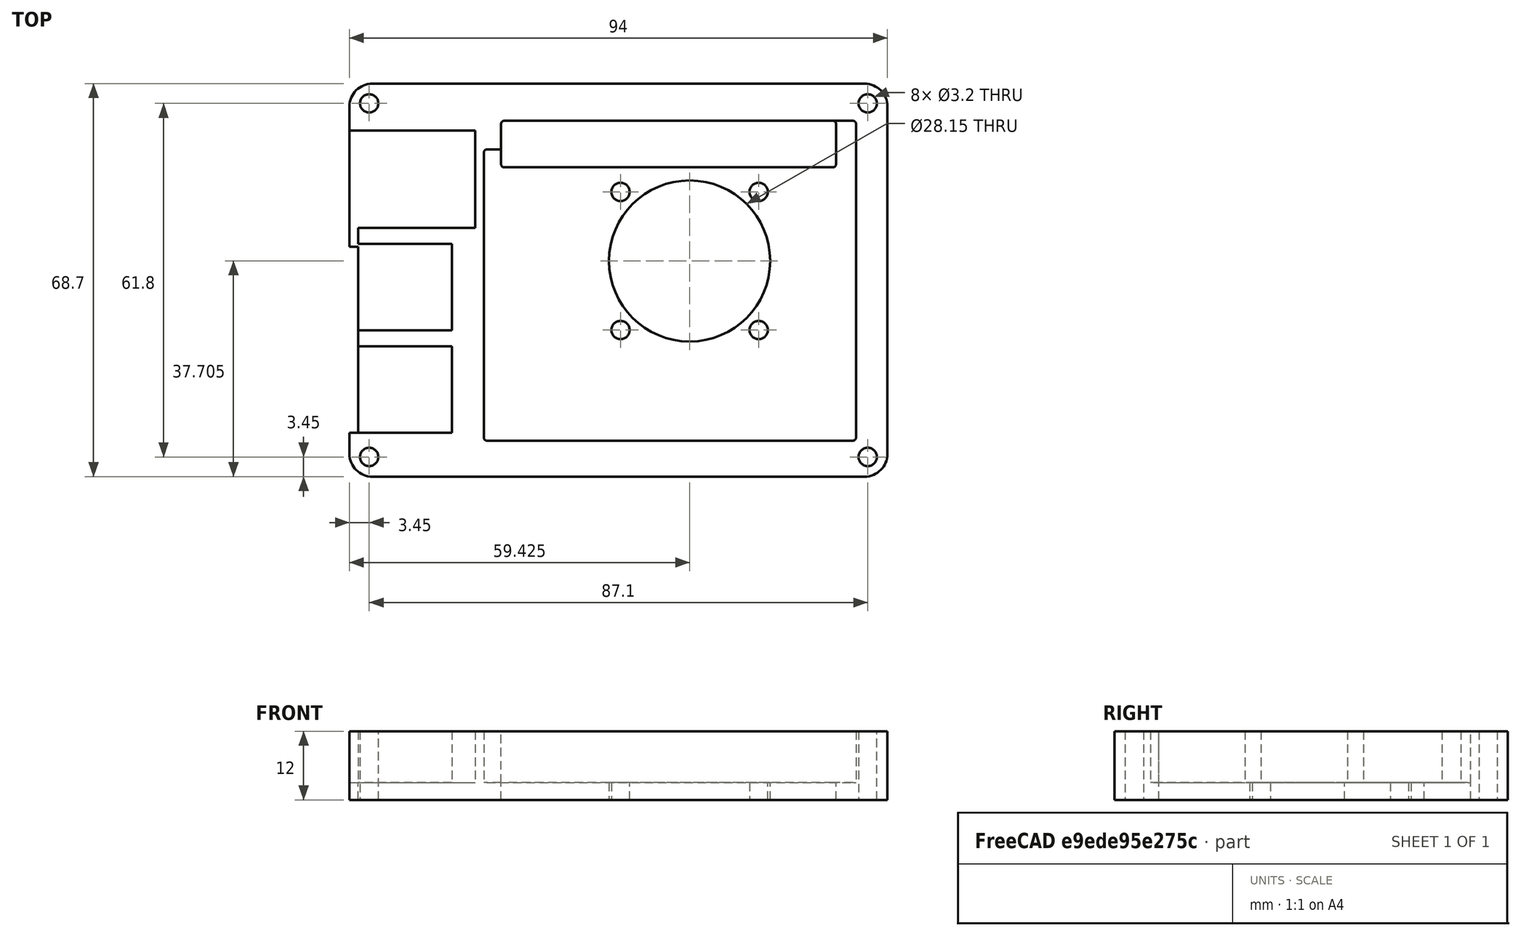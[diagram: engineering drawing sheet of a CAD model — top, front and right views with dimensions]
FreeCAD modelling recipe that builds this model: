
FCSTD DOCUMENT  (FreeCAD 0.19R24267 +148 (Git))
Label: 1. Lage
License: All rights reserved
LicenseURL: http://en.wikipedia.org/wiki/All_rights_reserved
objects: TechDraw::DrawViewDimension×21, TechDraw::DrawProjGroupItem×4, Sketcher::SketchObject×2, PartDesign::Fillet×2, PartDesign::Pad×1, PartDesign::Pocket×1, PartDesign::Body×1, TechDraw::DrawSVGTemplate×1, TechDraw::DrawProjGroup×1, TechDraw::DrawPage×1
note: 11 computed .brp shape members not serialized (recipe doc carries the construction recipe); baked Part::Feature solids carry a one-line shape summary decoded from their .brp

FEATURE [Sketcher::SketchObject] Sketch
  FullyConstrained = true
  MapMode = 5
  Support = -> [XY_Plane]
  sketch-geometry (29):
    g0: LineSegment StartX=0 StartY=0 StartZ=0 EndX=94 EndY=0 EndZ=0
    g1: LineSegment StartX=94 StartY=0 StartZ=0 EndX=94 EndY=68.7 EndZ=0
    g2: LineSegment StartX=94 StartY=68.7 StartZ=0 EndX=0 EndY=68.7 EndZ=0
    g3: Circle CenterX=3.45 CenterY=65.25 CenterZ=0 NormalX=0 NormalY=0 NormalZ=1 AngleXU=0 Radius=1.6
    g4: Circle CenterX=90.55 CenterY=65.25 CenterZ=0 NormalX=0 NormalY=0 NormalZ=1 AngleXU=0 Radius=1.6
    g5: Circle CenterX=90.55 CenterY=3.45 CenterZ=0 NormalX=0 NormalY=0 NormalZ=1 AngleXU=0 Radius=1.6
    g6: Circle CenterX=3.45 CenterY=3.45 CenterZ=0 NormalX=0 NormalY=0 NormalZ=1 AngleXU=0 Radius=1.6
    g7: GeomPoint X=47 Y=34.35 Z=0
    g8: LineSegment StartX=26.5 StartY=62.2 StartZ=0 EndX=85 EndY=62.2 EndZ=0
    g9: LineSegment StartX=85 StartY=62.2 StartZ=0 EndX=85 EndY=54.08 EndZ=0
    g10: LineSegment StartX=85 StartY=54.08 StartZ=0 EndX=26.5 EndY=54.08 EndZ=0
    g11: LineSegment StartX=26.5 StartY=54.08 StartZ=0 EndX=26.5 EndY=62.2 EndZ=0
    g12: LineSegment StartX=45.35 StartY=51.78 StartZ=0 EndX=73.5 EndY=51.78 EndZ=0
    g13: LineSegment StartX=73.5 StartY=51.78 StartZ=0 EndX=73.5 EndY=23.63 EndZ=0
    g14: LineSegment StartX=73.5 StartY=23.63 StartZ=0 EndX=45.35 EndY=23.63 EndZ=0
    g15: LineSegment StartX=45.35 StartY=23.63 StartZ=0 EndX=45.35 EndY=51.78 EndZ=0
    g16: Circle CenterX=59.425 CenterY=37.705 CenterZ=0 NormalX=0 NormalY=0 NormalZ=1 AngleXU=0 Radius=14.075
    g17: Circle CenterX=47.3512 CenterY=25.6312 CenterZ=0 NormalX=0 NormalY=0 NormalZ=1 AngleXU=0 Radius=1.6
    g18: Circle CenterX=71.4988 CenterY=25.6312 CenterZ=0 NormalX=0 NormalY=0 NormalZ=1 AngleXU=0 Radius=1.6
    g19: Circle CenterX=71.4988 CenterY=49.7788 CenterZ=0 NormalX=0 NormalY=0 NormalZ=1 AngleXU=0 Radius=1.6
    g20: Circle CenterX=47.3512 CenterY=49.7788 CenterZ=0 NormalX=0 NormalY=0 NormalZ=1 AngleXU=0 Radius=1.6
    g21: LineSegment StartX=45.35 StartY=51.78 StartZ=0 EndX=59.425 EndY=37.705 EndZ=0
    g22: GeomPoint X=48.4825 Y=48.6475 Z=0
    g23: GeomPoint X=49.4725 Y=47.6575 Z=0
    g24: LineSegment StartX=0 StartY=68.7 StartZ=0 EndX=0 EndY=40.2 EndZ=0
    g25: LineSegment StartX=0 StartY=40.2 StartZ=0 EndX=1.5 EndY=40.2 EndZ=0
    g26: LineSegment StartX=1.5 StartY=40.2 StartZ=0 EndX=1.5 EndY=7.7 EndZ=0
    g27: LineSegment StartX=1.5 StartY=7.7 StartZ=0 EndX=0 EndY=7.7 EndZ=0
    g28: LineSegment StartX=0 StartY=7.7 StartZ=0 EndX=0 EndY=0 EndZ=0
  constraints (76):
    c: Coincident(g0,g1)
    c: Coincident(g1,g2)
    c: Horizontal(g0)
    c: Horizontal(g2)
    c: Vertical(g1)
    c: Coincident(g0,g-1)
    c: DistanceY(g0,g2) = 68.7
    c: DistanceX(g2,g2) = 94
    c: Equal(g3,g4)
    c: Equal(g4,g6)
    c: Equal(g6,g5)
    c: Symmetric(g6,g4,g7)
    c: Symmetric(g5,g3,g7)
    c: Symmetric(g0,g2,g7)
    c: Horizontal(g6,g5)
    c: Vertical(g6,g3)
    c: Radius(g6) = 1.6
    c: DistanceY(g0,g6) = 3.45
    c: DistanceX(g0,g6) = 3.45
    c: Coincident(g8,g9)
    c: Coincident(g9,g10)
    c: Coincident(g10,g11)
    c: Coincident(g11,g8)
    c: Horizontal(g8)
    c: Horizontal(g10)
    c: Vertical(g9)
    c: Vertical(g11)
    c: DistanceY(g11,g11) = 8.12
    c: DistanceX(g8,g8) = 58.5
    c: DistanceY(g8,g1) = 6.5
    c: DistanceX(g8,g1) = 9
    c: Coincident(g12,g13)
    c: Coincident(g13,g14)
    c: Coincident(g14,g15)
    c: Coincident(g15,g12)
    c: Horizontal(g12)
    c: Horizontal(g14)
    c: Vertical(g13)
    c: Vertical(g15)
    c: Equal(g13,g14)
    c: Tangent(g16,g13)
    c: Symmetric(g12,g13,g16)
    c: Radius(g16) = 14.075
    c: DistanceY(g12,g9) = 2.3
    c: DistanceX(g13,g0) = 20.5
    c: Equal(g20,g17)
    c: Equal(g17,g18)
    c: Equal(g18,g19)
    c: Symmetric(g19,g17,g16)
    c: Symmetric(g18,g20,g16)
    c: Horizontal(g20,g19)
    c: Vertical(g20,g17)
    c: Coincident(g21,g12)
    c: Coincident(g21,g16)
    c: PointOnObject(g20,g21)
    c: PointOnObject(g22,g20)
    c: PointOnObject(g22,g21)
    c: PointOnObject(g23,g16)
    c: PointOnObject(g23,g21)
    c: Distance(g23,g22) = 1.4
    c: Radius(g20) = 1.6
    c: Equal(g2,g0)
    c: Coincident(g2,g24)
    c: Vertical(g24)
    c: Horizontal(g25)
    c: Coincident(g25,g26)
    c: Vertical(g26)
    c: Coincident(g26,g27)
    c: PointOnObject(g27,g-2)
    c: Horizontal(g27)
    c: Coincident(g27,g28)
    c: Coincident(g28,g0)
    c: Coincident(g25,g24)
    c: DistanceX(g25,g25) = 1.5
    c: DistanceY(g26,g26) = 32.5
    c: DistanceY(g24,g24) = 28.5
FEATURE [PartDesign::Pad] Pad
  Direction = (1,1,1)
  Length = 12
  Length2 = 100
  Profile = -> Sketch
  Type = 0
FEATURE [PartDesign::Fillet] Fillet
  Base = -> Pad [Edge26,Edge29,Edge32,Edge25]
  BaseFeature = -> Pad
  Radius = 0.5
  SupportTransform = false
FEATURE [PartDesign::Fillet] Fillet001
  Base = -> Fillet [Edge62,Edge61,Edge60,Edge59]
  BaseFeature = -> Fillet
  Radius = 4
  SupportTransform = false
FEATURE [Sketcher::SketchObject] Sketch001
  ExternalGeometry = -> [Fillet001]
  FullyConstrained = true
  MapMode = 5
  Placement = pos=(0,0,12) rot=(0,0,1;0rad)
  Support = -> [Fillet001]
  sketch-geometry (25):
    g0: LineSegment StartX=26.5 StartY=61.7 StartZ=0 EndX=26.5 EndY=57.2 EndZ=0
    g1: LineSegment StartX=24 StartY=6.3 StartZ=0 EndX=88 EndY=6.3 EndZ=0
    g2: LineSegment StartX=26.5 StartY=57.2 StartZ=0 EndX=24 EndY=57.2 EndZ=0
    g3: ArcOfCircle CenterX=24 CenterY=56.7 CenterZ=0 NormalX=0 NormalY=0 NormalZ=1 AngleXU=0 Radius=0.5 StartAngle=1.5708 EndAngle=3.14159
    g4: LineSegment StartX=23.5 StartY=56.7 StartZ=0 EndX=23.5 EndY=6.8 EndZ=0
    g5: ArcOfCircle CenterX=24 CenterY=6.8 CenterZ=0 NormalX=0 NormalY=0 NormalZ=1 AngleXU=0 Radius=0.5 StartAngle=3.14159 EndAngle=4.71239
    g6: ArcOfCircle CenterX=88 CenterY=6.8 CenterZ=0 NormalX=0 NormalY=0 NormalZ=1 AngleXU=0 Radius=0.5 StartAngle=4.71239 EndAngle=6.28319
    g7: LineSegment StartX=88.5 StartY=6.8 StartZ=0 EndX=88.5 EndY=61.7 EndZ=0
    g8: ArcOfCircle CenterX=88 CenterY=61.7 CenterZ=0 NormalX=0 NormalY=0 NormalZ=1 AngleXU=0 Radius=0.5 StartAngle=9e-16 EndAngle=1.5708
    g9: LineSegment StartX=88 StartY=62.2 StartZ=0 EndX=27 EndY=62.2 EndZ=0
    g10: ArcOfCircle CenterX=27 CenterY=61.7 CenterZ=0 NormalX=0 NormalY=0 NormalZ=1 AngleXU=0 Radius=0.5 StartAngle=1.5708 EndAngle=3.14159
    g11: LineSegment StartX=0 StartY=60.5 StartZ=0 EndX=22 EndY=60.5 EndZ=0
    g12: LineSegment StartX=22 StartY=60.5 StartZ=0 EndX=22 EndY=43.5 EndZ=0
    g13: LineSegment StartX=2e-16 StartY=40.2 StartZ=0 EndX=0 EndY=60.5 EndZ=0
    g14: LineSegment StartX=1.5 StartY=40.7 StartZ=0 EndX=17.9 EndY=40.7 EndZ=0
    g15: LineSegment StartX=17.9 StartY=40.7 StartZ=0 EndX=17.9 EndY=25.6 EndZ=0
    g16: LineSegment StartX=17.9 StartY=25.6 StartZ=0 EndX=1.5 EndY=25.6 EndZ=0
    g17: LineSegment StartX=1.5 StartY=22.8 StartZ=0 EndX=17.9 EndY=22.8 EndZ=0
    g18: LineSegment StartX=17.9 StartY=22.8 StartZ=0 EndX=17.9 EndY=7.7 EndZ=0
    g19: LineSegment StartX=17.9 StartY=7.7 StartZ=0 EndX=1.5 EndY=7.7 EndZ=0
    g20: LineSegment StartX=1.5 StartY=7.7 StartZ=0 EndX=1.5 EndY=22.8 EndZ=0
    g21: LineSegment StartX=2e-16 StartY=40.2 StartZ=0 EndX=1.5 EndY=40.2 EndZ=0
    g22: LineSegment StartX=1.5 StartY=43.5 StartZ=0 EndX=22 EndY=43.5 EndZ=0
    g23: LineSegment StartX=1.5 StartY=43.5 StartZ=0 EndX=1.5 EndY=40.7 EndZ=0
    g24: LineSegment StartX=1.5 StartY=40.2 StartZ=0 EndX=1.5 EndY=25.6 EndZ=0
  constraints (72):
    c: Vertical(g0)
    c: Horizontal(g1)
    c: Coincident(g0,g-9)
    c: Coincident(g0,g2)
    c: Horizontal(g2)
    c: Tangent(g2,g3) = -1.5708
    c: Coincident(g3,g4)
    c: Vertical(g4)
    c: Tangent(g4,g5) = -1.5708
    c: Coincident(g5,g1)
    c: Tangent(g1,g6) = -1.5708
    c: Coincident(g6,g7)
    c: Vertical(g7)
    c: Tangent(g7,g8) = -1.5708
    c: Coincident(g8,g9)
    c: Horizontal(g9)
    c: Tangent(g9,g10) = -1.5708
    c: Coincident(g10,g0)
    c: Coincident(g10,g-9)
    c: Equal(g3,g10)
    c: Equal(g5,g3)
    c: Equal(g3,g8)
    c: Equal(g8,g6)
    c: Vertical(g1,g5)
    c: Horizontal(g3,g3)
    c: Vertical(g8,g8)
    c: Horizontal(g6,g6)
    c: DistanceX(g6,g-7) = 5.5
    c: DistanceY(g-6,g1) = 6.3
    c: DistanceX(g3,g0) = 3
    c: DistanceY(g0,g-10) = 11.5
    c: Coincident(g11,g12)
    c: Coincident(g13,g11)
    c: Horizontal(g11)
    c: Vertical(g12)
    c: PointOnObject(g11,g-11)
    c: DistanceX(g11,g11) = 22
    c: DistanceY(g12,g12) = 17
    c: Coincident(g14,g15)
    c: Coincident(g15,g16)
    c: Horizontal(g14)
    c: Horizontal(g16)
    c: Vertical(g15)
    c: Coincident(g17,g18)
    c: Coincident(g18,g19)
    c: Coincident(g19,g20)
    c: Coincident(g20,g17)
    c: Horizontal(g17)
    c: Horizontal(g19)
    c: Vertical(g18)
    c: Vertical(g20)
    c: Coincident(g19,g-12)
    c: Equal(g15,g18)
    c: Equal(g17,g16)
    c: DistanceY(g18,g18) = 15.1
    c: DistanceY(g17,g15) = 2.8
    c: DistanceY(g14,g12) = 2.8
    c: DistanceX(g15,g4) = 5.6
    c: Vertical(g14,g17)
    c: Horizontal(g21)
    c: Coincident(g21,g-11)
    c: Vertical(g21,g-12)
    c: Coincident(g22,g12)
    c: Horizontal(g22)
    c: Coincident(g21,g13)
    c: Coincident(g23,g22)
    c: Coincident(g23,g14)
    c: Vertical(g23)
    c: Coincident(g24,g16)
    c: Vertical(g24)
    c: Vertical(g16,g17)
    c: Horizontal(g24,g13)
FEATURE [PartDesign::Pocket] Pocket
  BaseFeature = -> Fillet001
  Length = 9
  Length2 = 100
  Profile = -> Sketch001
  Type = 0
FEATURE [PartDesign::Body] Body
  Group = -> [Sketch,Pad,Fillet,Fillet001,Sketch001,Pocket]
  Origin = -> Origin
  Tip = -> Pocket
FEATURE [TechDraw::DrawSVGTemplate] Template
  EditableTexts = Designed_by_Name=David Völlm; Drawing_number=Drawing number; FC-Date=23.05.2023; FC-SC=Scale; FC-SH=Sheet; FC-Title=Raspberry Pi Gehäuse; Subtitle=Subtitle; Weight=Weight
  Height = 210
  Orientation = 1
  Width = 297
FEATURE [TechDraw::DrawProjGroupItem] ProjItem  label="Front"
  CoarseView = false
  Direction = (0,0,1)
  Focus = 100
  HardHidden = false
  IsoCount = 0
  IsoHidden = false
  IsoVisible = false
  LockPosition = true
  Perspective = false
  Rotation = 0
  RotationVector = (1,0,0)
  Scale = 0.5
  ScaleType = 2
  SeamHidden = false
  SeamVisible = true
  SmoothHidden = false
  SmoothVisible = true
  Source = -> [Body]
  Type = 0
  X = 0
  XDirection = (1,0,0)
  Y = 0
FEATURE [TechDraw::DrawProjGroupItem] ProjItem001  label="Left"
  CoarseView = false
  Direction = (-1,0,1e-16)
  Focus = 100
  HardHidden = false
  IsoCount = 0
  IsoHidden = false
  IsoVisible = false
  LockPosition = false
  Perspective = false
  Rotation = 0
  RotationVector = (1,0,0)
  ScaleType = 2
  SeamHidden = false
  SeamVisible = true
  SmoothHidden = false
  SmoothVisible = true
  Source = -> [Body]
  Type = 1
  X = 65.2243
  XDirection = (1e-16,0,1)
  Y = 0
FEATURE [TechDraw::DrawProjGroupItem] ProjItem002  label="Bottom"
  CoarseView = false
  Direction = (0,-1,0)
  Focus = 100
  HardHidden = false
  IsoCount = 0
  IsoHidden = false
  IsoVisible = false
  LockPosition = false
  Perspective = false
  Rotation = 0
  RotationVector = (1,0,0)
  ScaleType = 2
  SeamHidden = false
  SeamVisible = true
  SmoothHidden = false
  SmoothVisible = true
  Source = -> [Body]
  Type = 5
  X = 0
  XDirection = (1,0,0)
  Y = 35.175
FEATURE [TechDraw::DrawProjGroupItem] ProjItem003  label="Top"
  CoarseView = false
  Direction = (0,1,0)
  Focus = 100
  HardHidden = false
  IsoCount = 0
  IsoHidden = false
  IsoVisible = false
  LockPosition = false
  Perspective = false
  Rotation = 0
  RotationVector = (1,0,0)
  ScaleType = 2
  SeamHidden = false
  SeamVisible = true
  SmoothHidden = false
  SmoothVisible = true
  Source = -> [Body]
  Type = 4
  X = 0
  XDirection = (1,0,0)
  Y = -55.5576
FEATURE [TechDraw::DrawProjGroup] ProjGroup
  Anchor = -> ProjItem
  AutoDistribute = true
  LockPosition = false
  ProjectionType = 0
  Rotation = 0
  Scale = 0.5
  ScaleType = 2
  Source = -> [Body]
  Views = -> [ProjItem,ProjItem001,ProjItem002,ProjItem003]
  X = 107.356
  Y = 128.807
  spacingX = 15
  spacingY = 15
FEATURE [TechDraw::DrawViewDimension] Dimension001
  Arbitrary = false
  ArbitraryTolerances = false
  EqualTolerance = true
  FormatSpec = R%.2f
  FormatSpecOverTolerance = %+.2f
  FormatSpecUnderTolerance = %+.2f
  Inverted = false
  LockPosition = false
  MeasureType = 1
  OverTolerance = 0
  References2D = -> [ProjItem]
  Rotation = 0
  ScaleType = 0
  TheoreticalExact = false
  Type = 4
  UnderTolerance = 0
  X = -37.7748
  Y = 24.8617
FEATURE [TechDraw::DrawViewDimension] Dimension004
  Arbitrary = false
  ArbitraryTolerances = false
  EqualTolerance = true
  FormatSpec = %.2f
  FormatSpecOverTolerance = %+.2f
  FormatSpecUnderTolerance = %+.2f
  Inverted = false
  LockPosition = false
  MeasureType = 1
  OverTolerance = 0
  References2D = -> [ProjItem]
  Rotation = 0
  ScaleType = 0
  TheoreticalExact = false
  Type = 2
  UnderTolerance = 0
  X = -33.4357
  Y = -8.97918
FEATURE [TechDraw::DrawViewDimension] Dimension005
  Arbitrary = false
  ArbitraryTolerances = false
  EqualTolerance = true
  FormatSpec = %.2f
  FormatSpecOverTolerance = %+.2f
  FormatSpecUnderTolerance = %+.2f
  Inverted = false
  LockPosition = false
  MeasureType = 1
  OverTolerance = 0
  References2D = -> [ProjItem]
  Rotation = 0
  ScaleType = 0
  TheoreticalExact = false
  Type = 2
  UnderTolerance = 0
  X = -41.6257
  Y = -9.94553
FEATURE [TechDraw::DrawViewDimension] Dimension006
  Arbitrary = false
  ArbitraryTolerances = false
  EqualTolerance = true
  FormatSpec = %.2f
  FormatSpecOverTolerance = %+.2f
  FormatSpecUnderTolerance = %+.2f
  Inverted = false
  LockPosition = false
  MeasureType = 1
  OverTolerance = 0
  References2D = -> [ProjItem]
  Rotation = 0
  ScaleType = 0
  TheoreticalExact = false
  Type = 2
  UnderTolerance = 0
  X = -50.9328
  Y = -9.45354
FEATURE [TechDraw::DrawViewDimension] Dimension007
  Arbitrary = false
  ArbitraryTolerances = false
  EqualTolerance = true
  FormatSpec = %.2f
  FormatSpecOverTolerance = %+.2f
  FormatSpecUnderTolerance = %+.2f
  Inverted = false
  LockPosition = false
  MeasureType = 1
  OverTolerance = 0
  References2D = -> [ProjItem]
  Rotation = 0
  ScaleType = 0
  TheoreticalExact = false
  Type = 2
  UnderTolerance = 0
  X = -60.5795
  Y = -7.78573
FEATURE [TechDraw::DrawViewDimension] Dimension008
  Arbitrary = false
  ArbitraryTolerances = false
  EqualTolerance = true
  FormatSpec = %.2f
  FormatSpecOverTolerance = %+.2f
  FormatSpecUnderTolerance = %+.2f
  Inverted = false
  LockPosition = false
  MeasureType = 1
  OverTolerance = 0
  References2D = -> [ProjItem]
  Rotation = 0
  ScaleType = 0
  TheoreticalExact = false
  Type = 2
  UnderTolerance = 0
  X = -68.2439
  Y = -1.67489
FEATURE [TechDraw::DrawViewDimension] Dimension009
  Arbitrary = false
  ArbitraryTolerances = false
  EqualTolerance = true
  FormatSpec = %.2f
  FormatSpecOverTolerance = %+.2f
  FormatSpecUnderTolerance = %+.2f
  Inverted = false
  LockPosition = false
  MeasureType = 1
  OverTolerance = 0
  References2D = -> [ProjItem]
  Rotation = 0
  ScaleType = 0
  TheoreticalExact = false
  Type = 2
  UnderTolerance = 0
  X = -75.0941
  Y = 1.25365
FEATURE [TechDraw::DrawViewDimension] Dimension010
  Arbitrary = false
  ArbitraryTolerances = false
  EqualTolerance = true
  FormatSpec = %.2f
  FormatSpecOverTolerance = %+.2f
  FormatSpecUnderTolerance = %+.2f
  Inverted = false
  LockPosition = false
  MeasureType = 1
  OverTolerance = 0
  References2D = -> [ProjItem]
  Rotation = 0
  ScaleType = 0
  TheoreticalExact = false
  Type = 2
  UnderTolerance = 0
  X = -85.8551
  Y = 2.37863
FEATURE [TechDraw::DrawViewDimension] Dimension
  Arbitrary = false
  ArbitraryTolerances = false
  EqualTolerance = true
  FormatSpec = R%.2f
  FormatSpecOverTolerance = %+.2f
  FormatSpecUnderTolerance = %+.2f
  Inverted = false
  LockPosition = false
  MeasureType = 1
  OverTolerance = 0
  References2D = -> [ProjItem]
  Rotation = 0
  ScaleType = 0
  TheoreticalExact = false
  Type = 4
  UnderTolerance = 0
  X = -4.5884
  Y = -4.5884
FEATURE [TechDraw::DrawViewDimension] Dimension011
  Arbitrary = false
  ArbitraryTolerances = false
  EqualTolerance = true
  FormatSpec = R%.2f
  FormatSpecOverTolerance = %+.2f
  FormatSpecUnderTolerance = %+.2f
  Inverted = false
  LockPosition = false
  MeasureType = 1
  OverTolerance = 0
  References2D = -> [ProjItem]
  Rotation = 0
  ScaleType = 0
  TheoreticalExact = false
  Type = 4
  UnderTolerance = 0
  X = -30.5037
  Y = 29.4025
FEATURE [TechDraw::DrawViewDimension] Dimension012
  Arbitrary = false
  ArbitraryTolerances = false
  EqualTolerance = true
  FormatSpec = %.2f
  FormatSpecOverTolerance = %+.2f
  FormatSpecUnderTolerance = %+.2f
  Inverted = false
  LockPosition = false
  MeasureType = 1
  OverTolerance = 0
  References2D = -> [ProjItem]
  Rotation = 0
  ScaleType = 0
  TheoreticalExact = false
  Type = 1
  UnderTolerance = 0
  X = -17.9238
  Y = -17.884
FEATURE [TechDraw::DrawViewDimension] Dimension013
  Arbitrary = false
  ArbitraryTolerances = false
  EqualTolerance = true
  FormatSpec = %.2f
  FormatSpecOverTolerance = %+.2f
  FormatSpecUnderTolerance = %+.2f
  Inverted = false
  LockPosition = false
  MeasureType = 1
  OverTolerance = 0
  References2D = -> [ProjItem]
  Rotation = 0
  ScaleType = 0
  TheoreticalExact = false
  Type = 1
  UnderTolerance = 0
  X = -34.8486
  Y = -24.0207
FEATURE [TechDraw::DrawViewDimension] Dimension014
  Arbitrary = false
  ArbitraryTolerances = false
  EqualTolerance = true
  FormatSpec = %.2f
  FormatSpecOverTolerance = %+.2f
  FormatSpecUnderTolerance = %+.2f
  Inverted = false
  LockPosition = false
  MeasureType = 1
  OverTolerance = 0
  References2D = -> [ProjItem]
  Rotation = 0
  ScaleType = 0
  TheoreticalExact = false
  Type = 1
  UnderTolerance = 0
  X = -35.2445
  Y = -29.4515
FEATURE [TechDraw::DrawViewDimension] Dimension015
  Arbitrary = false
  ArbitraryTolerances = false
  EqualTolerance = true
  FormatSpec = %.2f
  FormatSpecOverTolerance = %+.2f
  FormatSpecUnderTolerance = %+.2f
  Inverted = false
  LockPosition = false
  MeasureType = 1
  OverTolerance = 0
  References2D = -> [ProjItem]
  Rotation = 0
  ScaleType = 0
  TheoreticalExact = false
  Type = 1
  UnderTolerance = 0
  X = -37.5118
  Y = -35.1447
FEATURE [TechDraw::DrawViewDimension] Dimension016
  Arbitrary = false
  ArbitraryTolerances = false
  EqualTolerance = true
  FormatSpec = R%.2f
  FormatSpecOverTolerance = %+.2f
  FormatSpecUnderTolerance = %+.2f
  Inverted = false
  LockPosition = false
  MeasureType = 1
  OverTolerance = 0
  References2D = -> [ProjItem]
  Rotation = 0
  ScaleType = 0
  TheoreticalExact = false
  Type = 4
  UnderTolerance = 0
  X = 4.63228
  Y = 26.3461
FEATURE [TechDraw::DrawViewDimension] Dimension017
  Arbitrary = false
  ArbitraryTolerances = false
  EqualTolerance = true
  FormatSpec = %.2f
  FormatSpecOverTolerance = %+.2f
  FormatSpecUnderTolerance = %+.2f
  Inverted = false
  LockPosition = false
  MeasureType = 1
  OverTolerance = 0
  References2D = -> [ProjItem]
  Rotation = 0
  ScaleType = 0
  TheoreticalExact = false
  Type = 1
  UnderTolerance = 0
  X = -12.942
  Y = -41.6356
FEATURE [TechDraw::DrawViewDimension] Dimension018
  Arbitrary = false
  ArbitraryTolerances = false
  EqualTolerance = true
  FormatSpec = %.2f
  FormatSpecOverTolerance = %+.2f
  FormatSpecUnderTolerance = %+.2f
  Inverted = false
  LockPosition = false
  MeasureType = 1
  OverTolerance = 0
  References2D = -> [ProjItem]
  Rotation = 0
  ScaleType = 0
  TheoreticalExact = false
  Type = 1
  UnderTolerance = 0
  X = -0.072172
  Y = -47.1905
FEATURE [TechDraw::DrawViewDimension] Dimension019
  Arbitrary = false
  ArbitraryTolerances = false
  EqualTolerance = true
  FormatSpec = %.2f
  FormatSpecOverTolerance = %+.2f
  FormatSpecUnderTolerance = %+.2f
  Inverted = false
  LockPosition = false
  MeasureType = 1
  OverTolerance = 0
  References2D = -> [ProjItem]
  Rotation = 0
  ScaleType = 0
  TheoreticalExact = false
  Type = 1
  UnderTolerance = 0
  X = 3.18469
  Y = -52.957
FEATURE [TechDraw::DrawViewDimension] Dimension020
  Arbitrary = false
  ArbitraryTolerances = false
  EqualTolerance = true
  FormatSpec = %.2f
  FormatSpecOverTolerance = %+.2f
  FormatSpecUnderTolerance = %+.2f
  Inverted = false
  LockPosition = false
  MeasureType = 1
  OverTolerance = 0
  References2D = -> [ProjItem]
  Rotation = 0
  ScaleType = 0
  TheoreticalExact = false
  Type = 2
  UnderTolerance = 0
  X = 27.7972
  Y = 23.5117
FEATURE [TechDraw::DrawViewDimension] Dimension021
  Arbitrary = false
  ArbitraryTolerances = false
  EqualTolerance = true
  FormatSpec = %.2f
  FormatSpecOverTolerance = %+.2f
  FormatSpecUnderTolerance = %+.2f
  Inverted = false
  LockPosition = false
  MeasureType = 1
  OverTolerance = 0
  References2D = -> [ProjItem001]
  Rotation = 0
  ScaleType = 0
  TheoreticalExact = false
  Type = 1
  UnderTolerance = 0
  X = -13.3467
  Y = -22.9894
FEATURE [TechDraw::DrawViewDimension] Dimension022
  Arbitrary = false
  ArbitraryTolerances = false
  EqualTolerance = true
  FormatSpec = %.2f
  FormatSpecOverTolerance = %+.2f
  FormatSpecUnderTolerance = %+.2f
  Inverted = false
  LockPosition = false
  MeasureType = 1
  OverTolerance = 0
  References2D = -> [ProjItem001]
  Rotation = 0
  ScaleType = 0
  TheoreticalExact = false
  Type = 1
  UnderTolerance = 0
  X = -13.4824
  Y = -15.9107
FEATURE [TechDraw::DrawPage] Page
  KeepUpdated = true
  NextBalloonIndex = 1
  ProjectionType = 0
  Template = -> Template
  Views = -> [ProjGroup,Dimension001,Dimension004,Dimension005,Dimension006,Dimension007,Dimension008,Dimension009,Dimension010,Dimension,Dimension011,Dimension012,Dimension013,Dimension014,Dimension015,Dimension016,Dimension017,Dimension018,Dimension019,Dimension020,Dimension021,Dimension022]
